# Revit family: Haworth_Cabana_MeetingBox_EU_PRELIMINARY
name_source: partatom
category: Furniture
units: mm (PartAtom-declared; Revit-internal decimal feet)

## family parameters
Always vertical = Yes
Cut with Voids When Loaded = No
OmniClass Number = 23.40.70.14.64.21
OmniClass Title = Systems Furniture
Room Calculation Point = No
Shared = No
Work Plane-Based = No

## types (2) — shared parameters
Actual Depth = 250 cm
Actual Height = 137 cm
Assembly Code = E2020200
Description = Haworth - Cabana - Meeting Box
Manufacturer = Haworth
Model = Haworth - Cabana
Revision Number = 1
Size = Verify Final Dim. w/ Haworth
TV Mount = Yes
TV Mount Finish = Haworth _ Paint _ Metallic Silver
Trim Finish = Haworth _ Paint _ Plaster
URL = https://www.haworth.com
URL - Product = https://www.haworth.com
Warranty = http://www.haworth.com

## per-type parameters (varying)
| type | Actual Width | One Seat | Two Seats |
| One Seat | 98 cm | Yes | No |
| Two Seats | 188 cm | No | Yes |

## geometry (parser evidence)
native form markers: Extrusion x3, Sweep x19
no freeform markers — native parametric forms only
